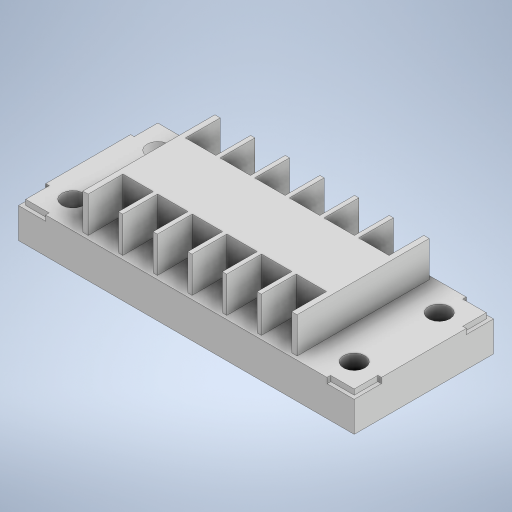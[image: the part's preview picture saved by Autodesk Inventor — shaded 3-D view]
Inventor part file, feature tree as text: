
AUTODESK INVENTOR PART (.ipt)
format: ipt  version: 2024 (Build 280153000, 153)  size: 364,032 bytes
history: native  units: in
note: dims shown in document units (in); Inventor stores cm internally (conversion verified against a paired STEP export)
features: sketch x5, extrude x4, mirror x2, pattern_linear x1, hole x1
ambient origin geometry x8: Origin, YZ Plane, XZ Plane, XY Plane, X Axis, Y Axis, Z Axis, Center Point
bodies: Solid1 (feature_tree)
feature tree (13):
  extrude  "Extrusion1"  Depth=4.7in
  extrude  "Extrusion2"  Depth=1.95in
  extrude  "Extrusion3"  Depth=0.85in
  pattern_linear  "Rectangular Pattern1"  Spacing1=1.85in  [1 undecoded]
  extrude  "Extrusion4"  Depth=0.85in
  mirror  "Mirror1"
  hole  "Hole1"  [1 undecoded]
  mirror  "Mirror2"
  sketch  "Sketch1"  dims[d0=4.7in d1=2.35in]
  sketch  "Sketch2"  dims[d2=1.95in d3=0.975in]
  sketch  "Sketch3"  dims[d4=0.5in d5=0.0in d6=0.85in]
  sketch  "Sketch4"  dims[d7=3.0in]
  sketch  "Sketch5"  dims[d8=0.05in d9=1.85in d10=0.85in d11=0.5in d12=0.0in d13=0.075in d14=0.425in d15=0.4375in d16=0.5in d17=0.0in d18=2.3622in d20=0.485in d21=0.7874in d23=-1.3625in d24=0.05in d25=0.05in d26=0.33in d27=0.05in d28=0.05in d29=0.075in d30=0.0in d31=0.3in d32=0.75in d33=0.375in d34=0.25in d35=0.5635in d36=1.0in d37=0.8108in d38=0.38in d39=0.38in d40=0.38in d41=0.38in]
note: 2 required parameter values undecoded (feature->parameter linkage not recoverable at this tier; creation-order binding heuristic only, values carry confidence <= 0.55)
